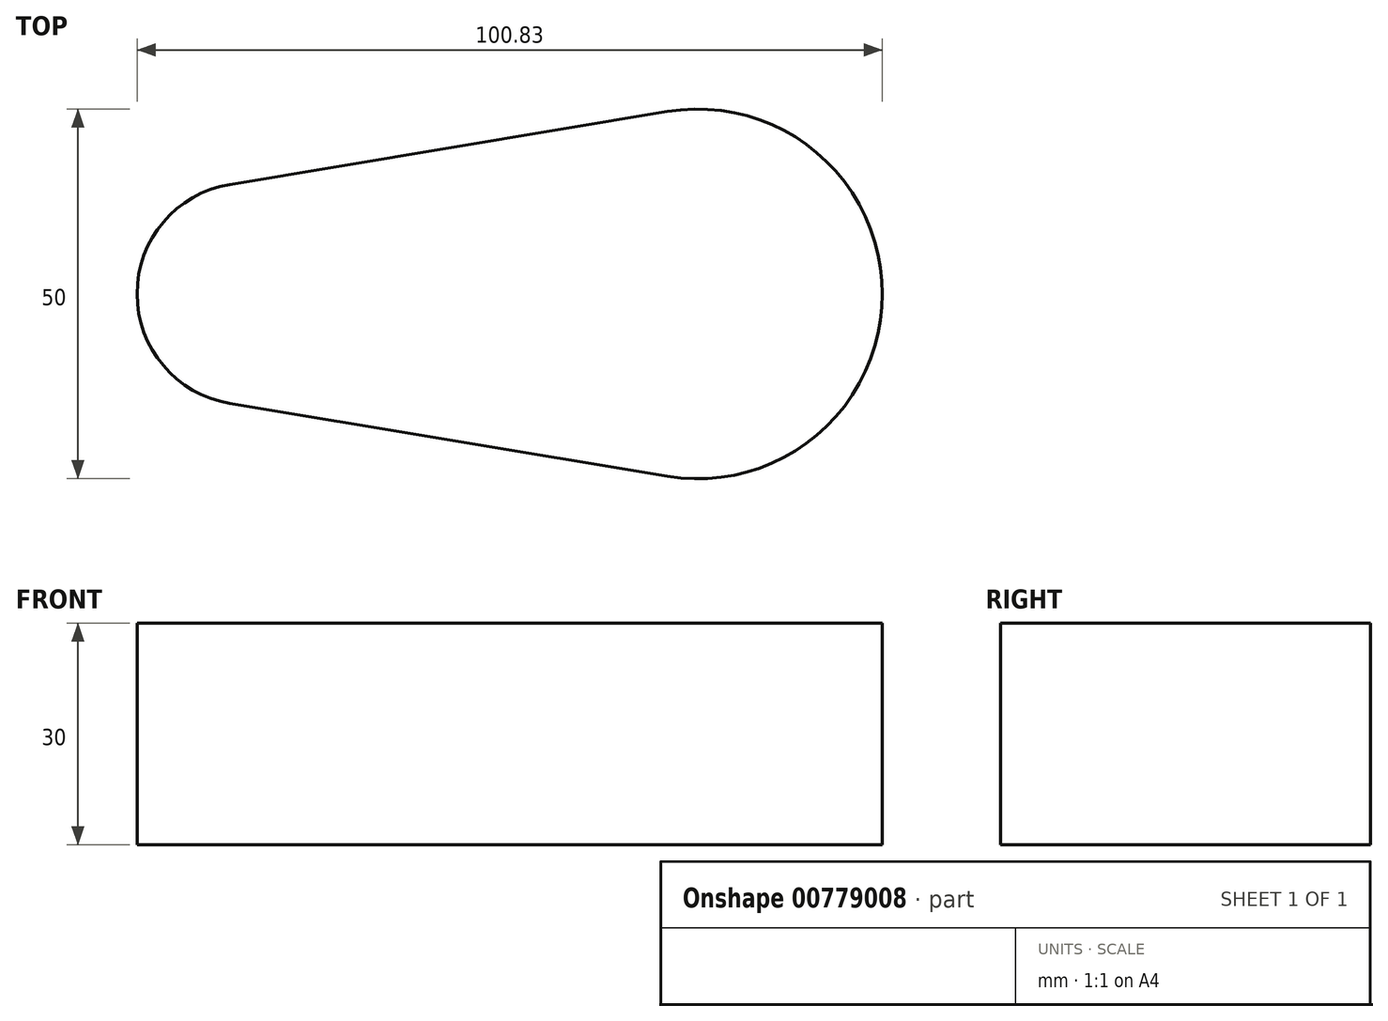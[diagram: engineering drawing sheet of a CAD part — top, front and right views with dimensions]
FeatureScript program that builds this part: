
annotation { "Feature Type Name" : "Feature", "Feature Type Description" : "" }
export const myFeature = defineFeature(function(context is Context, id is Id, definition is map)
    precondition{}
    {
        {
            var Q0;
            Q0=qCreatedBy(makeId("Top.planeOp"),FACE);
            var sketch = newSketch(context, id + "F0", { "sketchPlane" : qUnion([Q0])});
            skLineSegment(sketch, "E0", {"start": v(-59.18, 14.8) * mm, "end": v(0, 24.66) * mm});
            skArc(sketch, "E1", {"start": v(-59.18, 14.8) * mm, "mid": v(-71.72, 0) * mm, "end": v(-59.18, -14.8) * mm});
            skArc(sketch, "E2", {"start": v(0, -24.66) * mm, "mid": v(29.1, 0) * mm, "end": v(0, 24.66) * mm});
            skLineSegment(sketch, "E3", {"start": v(-105.43, 0) * mm, "end": v(101.13, 0) * mm, "construction": true});
            skLineSegment(sketch, "E4.MirrorCS", {"start": v(-59.18, -14.8) * mm, "end": v(0, -24.66) * mm});
            skSolve(sketch);
        }
        {
            var Q0;
            Q0 = qSketchRegion(id + "F0", true);
            extrude(context, id + "F1", {"entities" : qUnion([Q0]), "depth" : 30 * mm, "offsetDistance" : 25.4 * mm});
        }
    });
